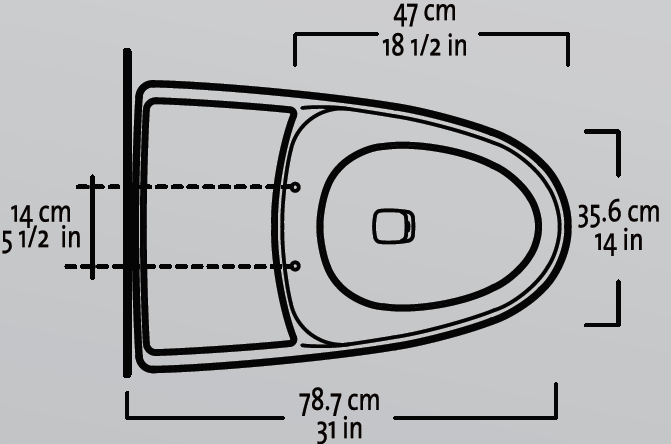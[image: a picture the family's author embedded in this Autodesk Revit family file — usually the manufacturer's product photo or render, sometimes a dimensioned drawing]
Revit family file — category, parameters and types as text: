
# Revit family: Sanit_1Pza_Prestigio_Alongado_Corona
name_source: partatom
category: Aparatos sanitarios
units: mm (PartAtom-declared; Revit-internal decimal feet)

## family parameters
Anfitrión = Suelo
Compartido = No
Corte con vacíos al cargar = No
Cota de conector redondo = Diámetro de uso
Número OmniClass = 23.31.19.17
Punto de cálculo de habitación = No
Siempre vertical = Sí
Tipo de pieza = Normal

## types (1)
- Sanit_1Pza_Prestigio_Alongado_Corona
    Acabado = Corona_100_Blanco
    Alto = 508 mm
    Ancho = 508 mm
    Creado por = IDD
    Descripción = Sofisticada silueta baja, sanitario alongado para mayor comodidad con altura tradicional de taza para uso familiar. Cumple especificaciones water sense lo que garantiza un óptimo funcionamiento del producto con menos agua que un sanitario convencional
    Diámetro abasto = 51 mm
    Diámetro desagüe = 13 mm
    Espejo de agua = 12 5/8 x 10 5/8 (32 x 27 cm).
    Fabricante = Corona
    Fecha de creación = 06/07/2020
    Garantía = Gatantía integral de por vida.
    Lugar de fabricación = Girardota - Cundinamarca.
    Material = Corona_Porcelana_Sanitaria
    Modelo = Prestigio
    Peso  Bruto = 115 lbs (52 kg).
    Presion_ = 25 a 125 psi
    Presión = 125.00 psi
    Profundidad = 787 mm
    Referencia = 306361001
    Sistema de descarga = Presión asistida Flush. Mate IV de Sloan.
    URL = https://corona.co

## geometry (parser evidence)
native form markers: Sweep x8
no freeform markers — native parametric forms only
